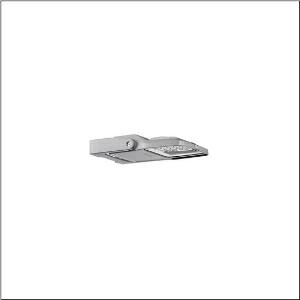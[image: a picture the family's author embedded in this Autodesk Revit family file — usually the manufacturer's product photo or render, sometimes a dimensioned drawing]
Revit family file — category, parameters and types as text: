
# Revit family: floodlight_fl_21_iq_micro___pl33t_5xa7762a2f2a_46b5
name_source: partatom
category: Lighting Fixtures
units: mm (PartAtom-declared; Revit-internal decimal feet)

## family parameters
Cut with Voids When Loaded = No
Host = Face
Light Source = No
Part Type = Normal
Room Calculation Point = No
Round Connector Dimension = Use Diameter
Shared = No

## types (1)
- --- (1 x LED, 2930 lm, 23.1 W, 3000K)
    Apparent Load = 23 VA
    CIE Flux Codes = 26 75 99 100 100
    Color Rendering = 70
    Color Temperature = 3000K
    Default Elevation = 1800 mm
    Description = Floodlight FL 21 iQ micro, floodlight, primary light control with lens, of PMMA, primary optical cover: protective disc, of toughened safety glass, transparent, light distribution: PL33T, light emission: direct distribution, installation type: surface-mounted, LED, High Power LED, rated luminous flux: 2.930lm, luminous efficacy: 127lm/W, light colour: 730, colour temperature: 3000K, control: Auto-Match, Temp-Guard, Night-Set, Smart-Wire, Desk-Remote (wireless, voltage-free reading and setting of iQ features in the workshop via application-optimized NFC function/RFID function), optimised constant luminous flux control (CLO 2.0), Street-Remote, with terminal, 6-pole, mains connection: 220..240V, AC, 50/60Hz, start of lifetime: 23W, end of service life: 24W, reduction: 11W, luminaire housing, of diecast aluminium, powder-coated, Siteco® metallic grey (DB 702S), corrosivity category C5 mid according to DIN EN ISO 12944, sealing non-destructively replaceable, design bracket, of diecast aluminium, powder-coated, Siteco® metallic grey (DB 702S), protection rating (complete): IP66, insulation class (complete): insulation class II (safety insulation), certification: CE, ENEC, VDE, protection symbol: D, impact resistance: IK07, permissible operating ambient temperature: -40..+40°C, permissible operating ambient temperature for outdoor applications: -40..+50°C, standard: DIN EN 12944, LABS conformity tested according to VDMA 24364:2018-05, packaging unit: 1 piece

Light Distribution: PL33T
    Height = 65 mm
    Lamp = 1 x LED
    Lamp Light Flux = 2930 lm
    Lamp Power = 23.1 W
    Lamp count = 1
    Length = 312 mm
    Luminous efficacy = 127 lm/W
    Manufacturer = Siteco
    ModVariant = No
    Model = 5XA7762A2F2A
    Mounting Place = Wall
    Mounting Type = Surface mounted
    Number of Poles = 1
    OnlyDefault = Yes
    Power Factor = 1
    Product Name = Floodlight FL 21 iQ micro | PL33T
    Product group = floodlight | wall mounted
    ProductGroupID = 2001
    Protection Class = Protection class II
    Protection Degree = IP 66
    RLX_Detail_Level = 1
    RLX_Emergency_Light_Flux = 0 lm
    RLX_Emergency_Type = 0
    RLX_Emergency_Type_DB = No
    RlxData = <blob elided: 97265 chars, md5=8cd3a70a>
    Socket = socket
    Standby Power = 0 W
    System Light Flux = 2930 lm
    System Power = 23 W
    Type Comments = factory setting: luminous flux: 100 % | dim-lin: 254 | 455 mA
    Type Image = l_1006878.jpg
    URL = http://relux.com
    VarID = @adj_118343
    Voltage = 0 V
    Weight = 0.00 kg
    Width = 230 mm

## geometry (parser evidence)
native form markers: Blend x4, Sweep x11
no freeform markers — native parametric forms only
